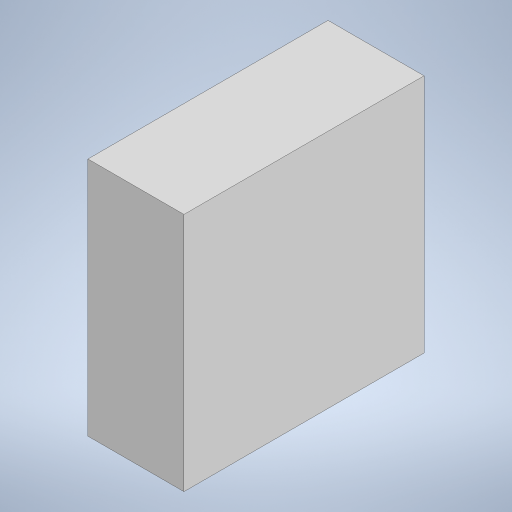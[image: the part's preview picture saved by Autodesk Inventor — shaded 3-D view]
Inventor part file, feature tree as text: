
AUTODESK INVENTOR PART (.ipt)
format: ipt  version: 2023 (Build 270158000, 158)  size: 226,304 bytes
history: native  units: mm
features: extrude x1, sketch x1
ambient origin geometry x8: Origin, YZ Plane, XZ Plane, XY Plane, X Axis, Y Axis, Z Axis, Center Point
bodies: Solid1 (feature_tree)
feature tree (2):
  extrude  "Extrusion1"  Depth=50.0mm
  sketch  "Sketch2"  dims[d0=20.0mm d1=50.0mm d2=50.0mm d3=0.0mm]
